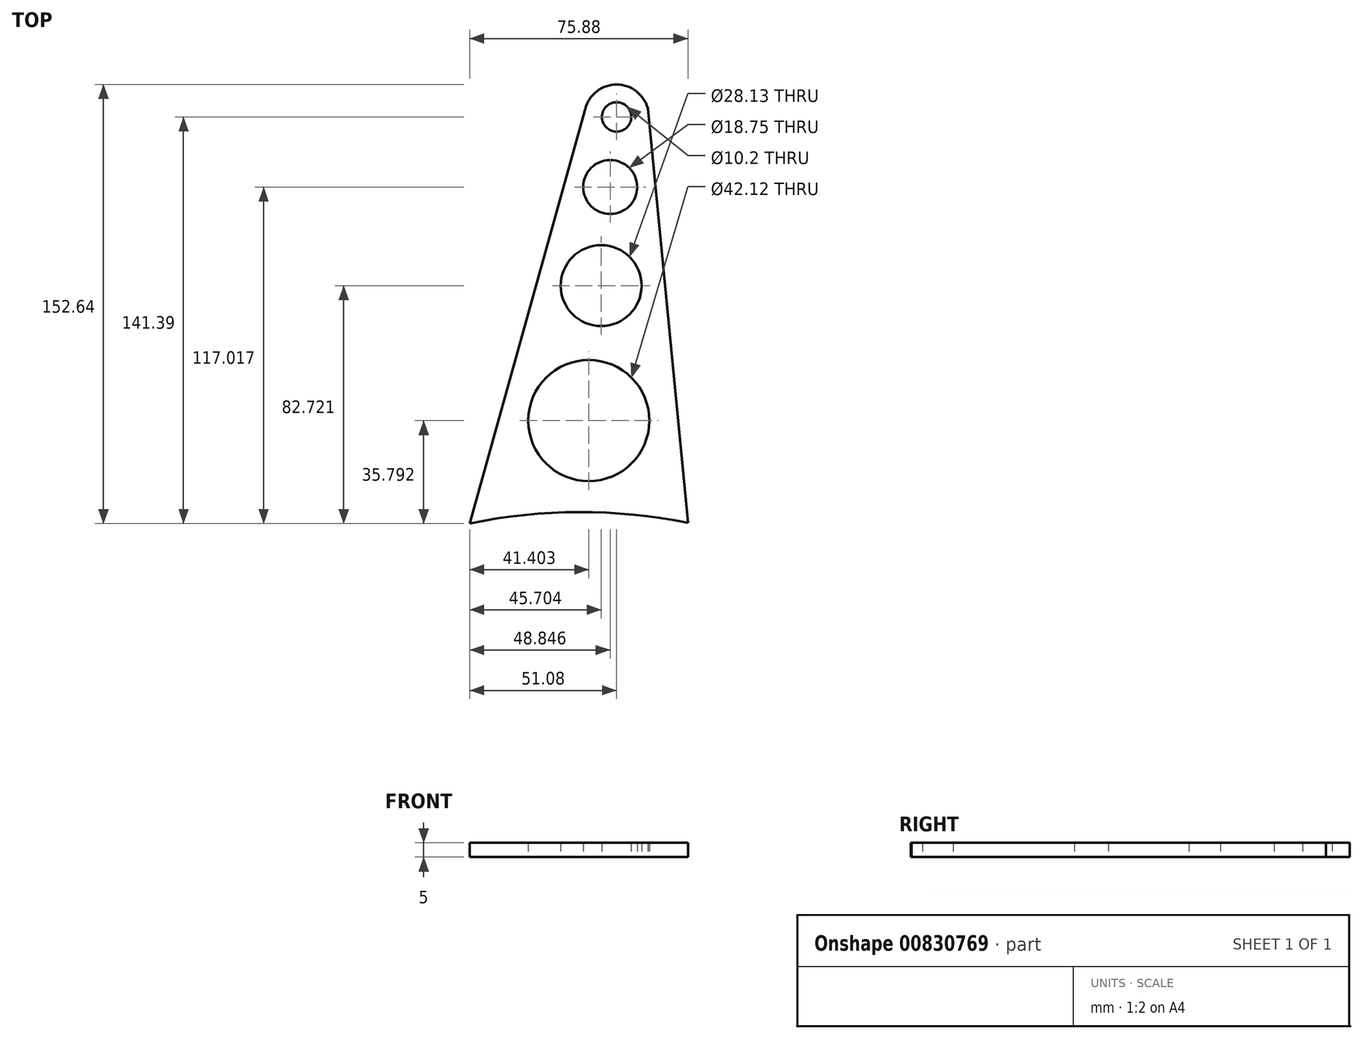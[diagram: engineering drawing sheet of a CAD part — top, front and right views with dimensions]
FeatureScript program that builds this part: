
annotation { "Feature Type Name" : "Feature", "Feature Type Description" : "" }
export const myFeature = defineFeature(function(context is Context, id is Id, definition is map)
    precondition{}
    {
        {
            var Q0;
            Q0=qCreatedBy(makeId("Top.planeOp"),FACE);
            var sketch = newSketch(context, id + "F0", { "sketchPlane" : qUnion([Q0])});
            skCircle(sketch, "E0", {"center": v(0, 0) * mm, "radius": 5.1 * mm});
            skArc(sketch, "E1", {"start": v(10.84, 3.02) * mm, "mid": v(0, 11.25) * mm, "end": v(-10.84, 3.02) * mm});
            skCircle(sketch, "E2", {"center": v(-2.23, -24.37) * mm, "radius": 9.38 * mm});
            skCircle(sketch, "E3", {"center": v(-5.38, -58.67) * mm, "radius": 14.06 * mm});
            skCircle(sketch, "E4", {"center": v(-9.68, -105.6) * mm, "radius": 21.06 * mm});
            skArc(sketch, "E5", {"start": v(24.8, -141.17) * mm, "mid": v(-13.15, -137.4) * mm, "end": v(-51.08, -141.4) * mm});
            skLineSegment(sketch, "E6", {"start": v(10.84, 3.02) * mm, "end": v(24.8, -141.17) * mm});
            skLineSegment(sketch, "E7", {"start": v(-10.84, 3.02) * mm, "end": v(-51.08, -141.4) * mm});
            skSolve(sketch);
        }
        {
            var Q0;
            Q0 = qSketchRegion(id + "F0", true);
            var Q1;
            Q1=makeQuery(id+"F0.imprint","IMPRINT",FACE,{"disambiguationData":[TD([[makeQuery(id+"F0.imprint","IMPRINT",EDGE,{"derivedFrom":sQuery(id+"F0.wireOp",EDGE,"E0")}),-1.0]])]});
            extrude(context, id + "F1", {"entities" : qUnion([Q0, Q1]), "depth" : 5 * mm, "offsetDistance" : 25 * mm});
        }
    });
